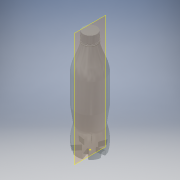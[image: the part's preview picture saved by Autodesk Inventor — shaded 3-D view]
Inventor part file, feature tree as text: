
AUTODESK INVENTOR PART (.ipt)
format: ipt  version: 2019 (Build 230136000, 136)  size: 608,256 bytes
history: native  units: in
note: dims shown in document units (in); Inventor stores cm internally (conversion verified against a paired STEP export)
features: sketch x9, extrude x5, fillet x4, revolve x2, projected_geometry x2, plane x1, chamfer x1
ambient origin geometry x8: Origin, YZ Plane, XZ Plane, XY Plane, X Axis, Y Axis, Z Axis, Center Point
bodies: Solid1 (feature_tree)
feature tree (24):
  extrude  "Extrusion1"  Depth=8.75in TaperAngle=0.0deg
  revolve  "Revolution1"  [1 undecoded]
  revolve  "Revolution2"  [1 undecoded]
  extrude  "Extrusion2"  TaperAngle=0.0deg  [1 undecoded]
  extrude  "Extrusion3"  Depth=5.5in
  fillet  "Fillet1"  Radius=7.0in
  plane  "Work Plane1"
  extrude  "Extrusion4"  Depth=1.0in
  chamfer  "Chamfer1"  Distance=2.0in
  extrude  "Extrusion5"  Depth=0.0625in
  fillet  "Fillet2"  Radius=0.2143in
  fillet  "Fillet3"  Radius=3.3786in
  fillet  "Fillet4"  Radius=0.5in
  sketch  "3D Sketch1"
  sketch  "Sketch9"  dims[d18=3.5in d20=2.0in d21=0.1in d22=0.2143in d24=3.3786in d25=0.5in d26=90.0deg d27=0.1374in d28=0.1374in d33=1.25in d34=0.75in d35=0.0in d36=0.075in d37=0.0in d38=-0.1875in d39=1.2in d40=0.02in d41=0.0in d42=0.625in d43=0.125in d44=0.0137in d45=0.1374in d46=0.1374in d47=2.3622in d49=360.0deg d51=0.5in d52=0.0in d56=0.0625in d57=0.0625in d58=0.0625in]
  sketch  "Sketch1"  dims[d0=2.5in d1=8.75in d2=0.0in]
  sketch  "Sketch2"  dims[d3=3.5in d4=0.125in]
  projected_geometry  "Projected Loop1"
  sketch  "Sketch3"  dims[d5=0.125in d7=2.5in]
  sketch  "Sketch5"  dims[d10=0.5in d11=0.0in]
  sketch  "Sketch6"  dims[d12=0.0505in d13=5.5in d14=7.0in]
  sketch  "Sketch7"  dims[d15=0.5in d16=1.0in]
  sketch  "Sketch8"  dims[d17=90.0deg]
  projected_geometry  "Project Cut Edges1"
note: 3 required parameter values undecoded (feature->parameter linkage not recoverable at this tier; creation-order binding heuristic only, values carry confidence <= 0.55)